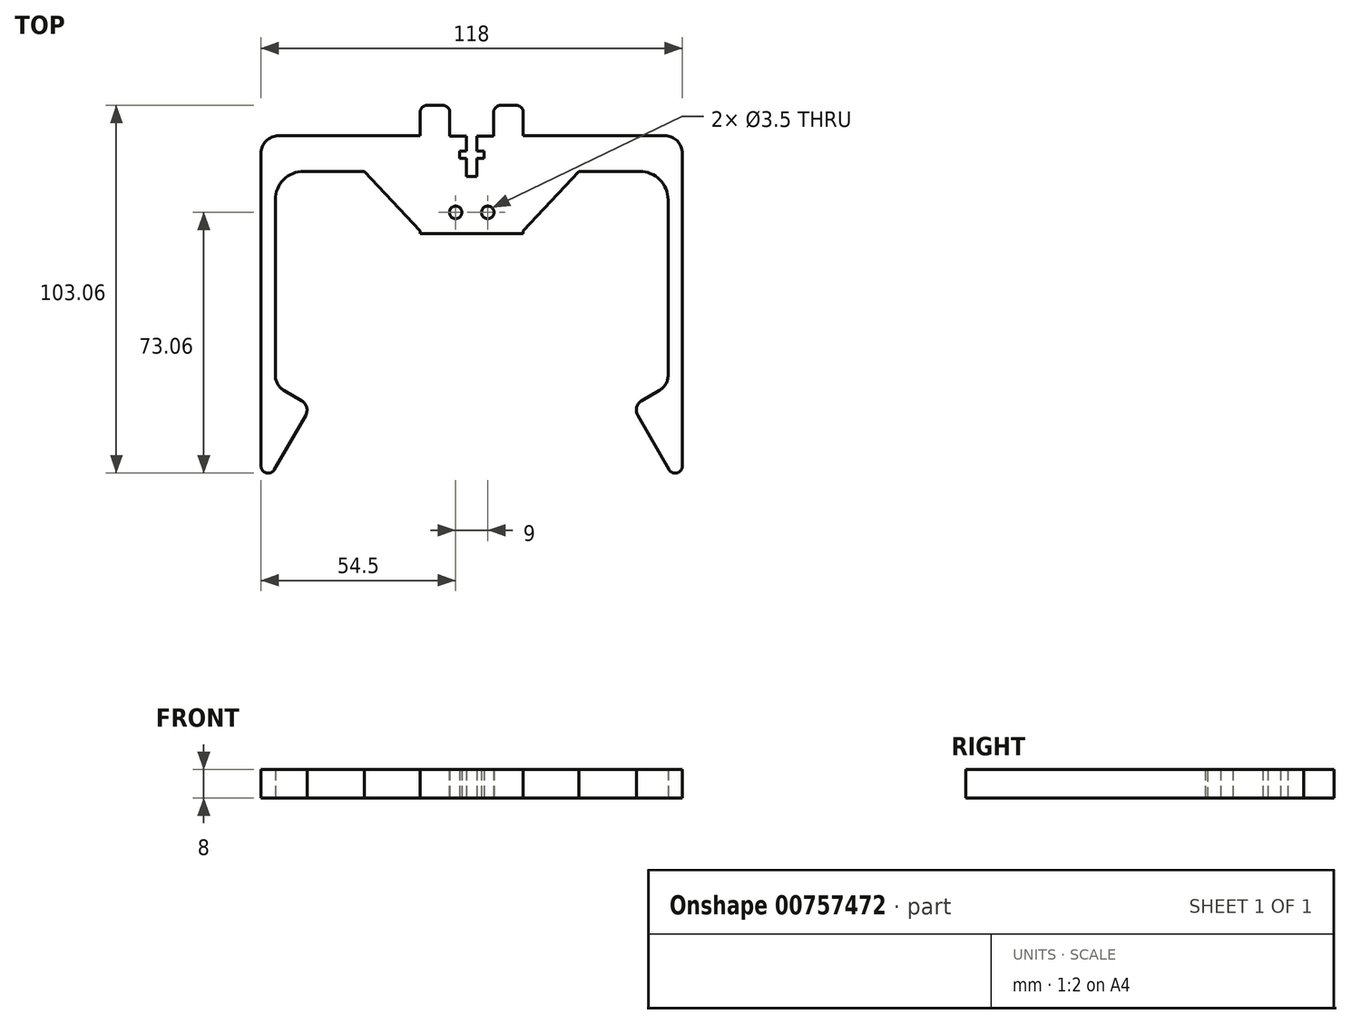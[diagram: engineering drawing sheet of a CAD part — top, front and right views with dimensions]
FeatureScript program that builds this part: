
annotation { "Feature Type Name" : "Feature", "Feature Type Description" : "" }
export const myFeature = defineFeature(function(context is Context, id is Id, definition is map)
    precondition{}
    {
        {
            var Q0;
            Q0=qCreatedBy(makeId("Top.planeOp"),FACE);
            var sketch = newSketch(context, id + "F0", { "sketchPlane" : qUnion([Q0])});
            skLineSegment(sketch, "E0", {"start": v(-12.45, -10) * mm, "end": v(-8.15, -10) * mm});
            skLineSegment(sketch, "E1", {"start": v(-6.15, -12) * mm, "end": v(-6.15, -18.6) * mm});
            skLineSegment(sketch, "E2", {"start": v(-6.15, -18.6) * mm, "end": v(-1.45, -18.6) * mm});
            skLineSegment(sketch, "E3", {"start": v(-1.45, -18.6) * mm, "end": v(-1.45, -22.9) * mm});
            skLineSegment(sketch, "E4", {"start": v(-1.45, -22.9) * mm, "end": v(-3.45, -22.9) * mm});
            skLineSegment(sketch, "E5", {"start": v(-3.45, -22.9) * mm, "end": v(-3.45, -24.9) * mm});
            skLineSegment(sketch, "E6", {"start": v(-3.45, -24.9) * mm, "end": v(-1.45, -24.9) * mm});
            skLineSegment(sketch, "E7", {"start": v(-1.45, -24.9) * mm, "end": v(-1.45, -29.9) * mm});
            skLineSegment(sketch, "E8", {"start": v(-1.45, -29.9) * mm, "end": v(1.45, -29.9) * mm});
            skLineSegment(sketch, "E9", {"start": v(1.45, -29.9) * mm, "end": v(1.45, -24.9) * mm});
            skLineSegment(sketch, "E10", {"start": v(1.45, -24.9) * mm, "end": v(3.45, -24.9) * mm});
            skLineSegment(sketch, "E11", {"start": v(3.45, -24.9) * mm, "end": v(3.45, -22.9) * mm});
            skLineSegment(sketch, "E12", {"start": v(3.45, -22.9) * mm, "end": v(1.45, -22.9) * mm});
            skLineSegment(sketch, "E13", {"start": v(1.45, -22.9) * mm, "end": v(1.45, -18.6) * mm});
            skLineSegment(sketch, "E14", {"start": v(1.45, -18.6) * mm, "end": v(6.15, -18.6) * mm});
            skLineSegment(sketch, "E15", {"start": v(6.15, -18.6) * mm, "end": v(6.15, -12) * mm});
            skLineSegment(sketch, "E16", {"start": v(8.15, -10) * mm, "end": v(12.45, -10) * mm});
            skLineSegment(sketch, "E17", {"start": v(14.45, -12) * mm, "end": v(14.45, -46) * mm});
            skLineSegment(sketch, "E18", {"start": v(14.45, -46) * mm, "end": v(-14.45, -46) * mm});
            skLineSegment(sketch, "E19", {"start": v(-14.45, -46) * mm, "end": v(-14.45, -12) * mm});
            skPoint(sketch, "E20.visualSharp", {"position": v(-14.45, -10) * mm});
            skArc(sketch, "E20.filletArc", {"start": v(-12.45, -10) * mm, "mid": v(-13.86, -10.59) * mm, "end": v(-14.45, -12) * mm});
            skPoint(sketch, "E21.visualSharp", {"position": v(-6.15, -10) * mm});
            skArc(sketch, "E21.filletArc", {"start": v(-6.15, -12) * mm, "mid": v(-6.74, -10.59) * mm, "end": v(-8.15, -10) * mm});
            skPoint(sketch, "E22.visualSharp", {"position": v(6.15, -10) * mm});
            skArc(sketch, "E22.filletArc", {"start": v(8.15, -10) * mm, "mid": v(6.74, -10.59) * mm, "end": v(6.15, -12) * mm});
            skPoint(sketch, "E23.visualSharp", {"position": v(14.45, -10) * mm});
            skArc(sketch, "E23.filletArc", {"start": v(14.45, -12) * mm, "mid": v(13.86, -10.59) * mm, "end": v(12.45, -10) * mm});
            skCircle(sketch, "E24", {"center": v(-4.5, -40) * mm, "radius": 1.75 * mm});
            skCircle(sketch, "E25", {"center": v(4.5, -40) * mm, "radius": 1.75 * mm});
            skSolve(sketch);
        }
        {
            var Q0;
            Q0=makeQuery(id+"F0.imprint","IMPRINT",FACE,{"disambiguationData":[TD([[makeQuery(id+"F0.imprint","IMPRINT",EDGE,{"derivedFrom":sQuery(id+"F0.wireOp",EDGE,"E0")}),-1.0]])]});
            extrude(context, id + "F1", {"entities" : qUnion([Q0]), "depth" : 8 * mm, "offsetDistance" : 25 * mm});
        }
        {
            var Q0;
            Q0=qCreatedBy(makeId("Top.planeOp"),FACE);
            var sketch = newSketch(context, id + "F2", { "sketchPlane" : qUnion([Q0])});
            skLineSegment(sketch, "E26", {"start": v(-10.84, -18.5) * mm, "end": v(-54, -18.5) * mm});
            skLineSegment(sketch, "E27", {"start": v(-59, -23.5) * mm, "end": v(-59, -111.06) * mm});
            skLineSegment(sketch, "E28", {"start": v(-55.27, -112.06) * mm, "end": v(-46.5, -96.87) * mm});
            skLineSegment(sketch, "E29", {"start": v(-47.6, -92.77) * mm, "end": v(-52.5, -89.94) * mm});
            skLineSegment(sketch, "E30", {"start": v(-55, -85.61) * mm, "end": v(-55, -36.5) * mm});
            skLineSegment(sketch, "E31", {"start": v(-47, -28.5) * mm, "end": v(-30, -28.5) * mm});
            skLineSegment(sketch, "E32", {"start": v(-30, -28.5) * mm, "end": v(-14.2, -45.5) * mm});
            skLineSegment(sketch, "E33", {"start": v(-14.2, -45.5) * mm, "end": v(-10.84, -18.5) * mm});
            skPoint(sketch, "E34.visualSharp", {"position": v(-55, -28.5) * mm});
            skArc(sketch, "E34.filletArc", {"start": v(-47, -28.5) * mm, "mid": v(-52.66, -30.84) * mm, "end": v(-55, -36.5) * mm});
            skPoint(sketch, "E35.visualSharp", {"position": v(-55, -88.5) * mm});
            skArc(sketch, "E35.filletArc", {"start": v(-55, -85.61) * mm, "mid": v(-54.33, -88.11) * mm, "end": v(-52.5, -89.94) * mm});
            skPoint(sketch, "E36.visualSharp", {"position": v(-45, -94.27) * mm});
            skArc(sketch, "E36.filletArc", {"start": v(-46.5, -96.87) * mm, "mid": v(-46.2, -94.6) * mm, "end": v(-47.6, -92.77) * mm});
            skPoint(sketch, "E37.visualSharp", {"position": v(-59, -118.52) * mm});
            skArc(sketch, "E37.filletArc", {"start": v(-59, -111.06) * mm, "mid": v(-57.52, -112.99) * mm, "end": v(-55.27, -112.06) * mm});
            skPoint(sketch, "E38.visualSharp", {"position": v(-59, -18.5) * mm});
            skArc(sketch, "E38.filletArc", {"start": v(-54, -18.5) * mm, "mid": v(-57.54, -19.96) * mm, "end": v(-59, -23.5) * mm});
            skSolve(sketch);
        }
        {
            var Q0;
            Q0=makeQuery(id+"F2.imprint","IMPRINT",FACE,{"disambiguationData":[TD([[makeQuery(id+"F2.imprint","IMPRINT",EDGE,{"derivedFrom":sQuery(id+"F2.wireOp",EDGE,"E26")}),1.0]])]});
            extrude(context, id + "F3", {"entities" : qUnion([Q0]), "depth" : 8 * mm, "offsetDistance" : 25 * mm});
        }
        {
            var Q0;
            Q0=makeQuery(id+"F3.opExtrude","SWEPT_BODY",BODY,{"disambiguationData":[OSD([sQuery(id+"F2.wireOp",EDGE,"E26"),sQuery(id+"F2.wireOp",EDGE,"Sv9c40Bs-9l0g-oEUb-zzUg-JlAZJcp3K7LD"),sQuery(id+"F2.wireOp",EDGE,"U6kETheJ-fzBR-YR6T-Lo92-pPjDwiqFGPaU"),sQuery(id+"F2.wireOp",EDGE,"fQB4OfuY-Hnde-KLL0-zR0P-CJxz8QV0w6S4"),sQuery(id+"F2.wireOp",EDGE,"A7Y2YME3-6kCl-aD6e-VmUe-T9eFmhLKAYnE"),sQuery(id+"F2.wireOp",EDGE,"E27"),sQuery(id+"F2.wireOp",EDGE,"E28"),sQuery(id+"F2.wireOp",EDGE,"E29"),sQuery(id+"F2.wireOp",EDGE,"E30"),sQuery(id+"F2.wireOp",EDGE,"G2XXry1L-lSBs-7qyM-IcOb-FJ39EMTVEb6M"),sQuery(id+"F2.wireOp",EDGE,"hQwfWFtU-uCWC-Zph9-OQmw-kL2zNpny13XQ"),sQuery(id+"F2.wireOp",EDGE,"anD41uHo-R6gk-uW85-v4Go-8DuhbWCkNCcU"),sQuery(id+"F2.wireOp",EDGE,"10dlnUwN-VAJH-UsSO-ae1m-CMNUUjCnu51U"),sQuery(id+"F2.wireOp",EDGE,"E31"),sQuery(id+"F2.wireOp",EDGE,"E32"),sQuery(id+"F2.wireOp",EDGE,"E33")])]});
            var Q1;
            Q1=qCreatedBy(makeId("Right.planeOp"),FACE);
            mirror(context, id + "F4", {"operationType" : NewBodyOperationType.ADD, "entities" : qUnion([Q0]), "mirrorPlane" : qUnion([Q1])});
        }
    });
